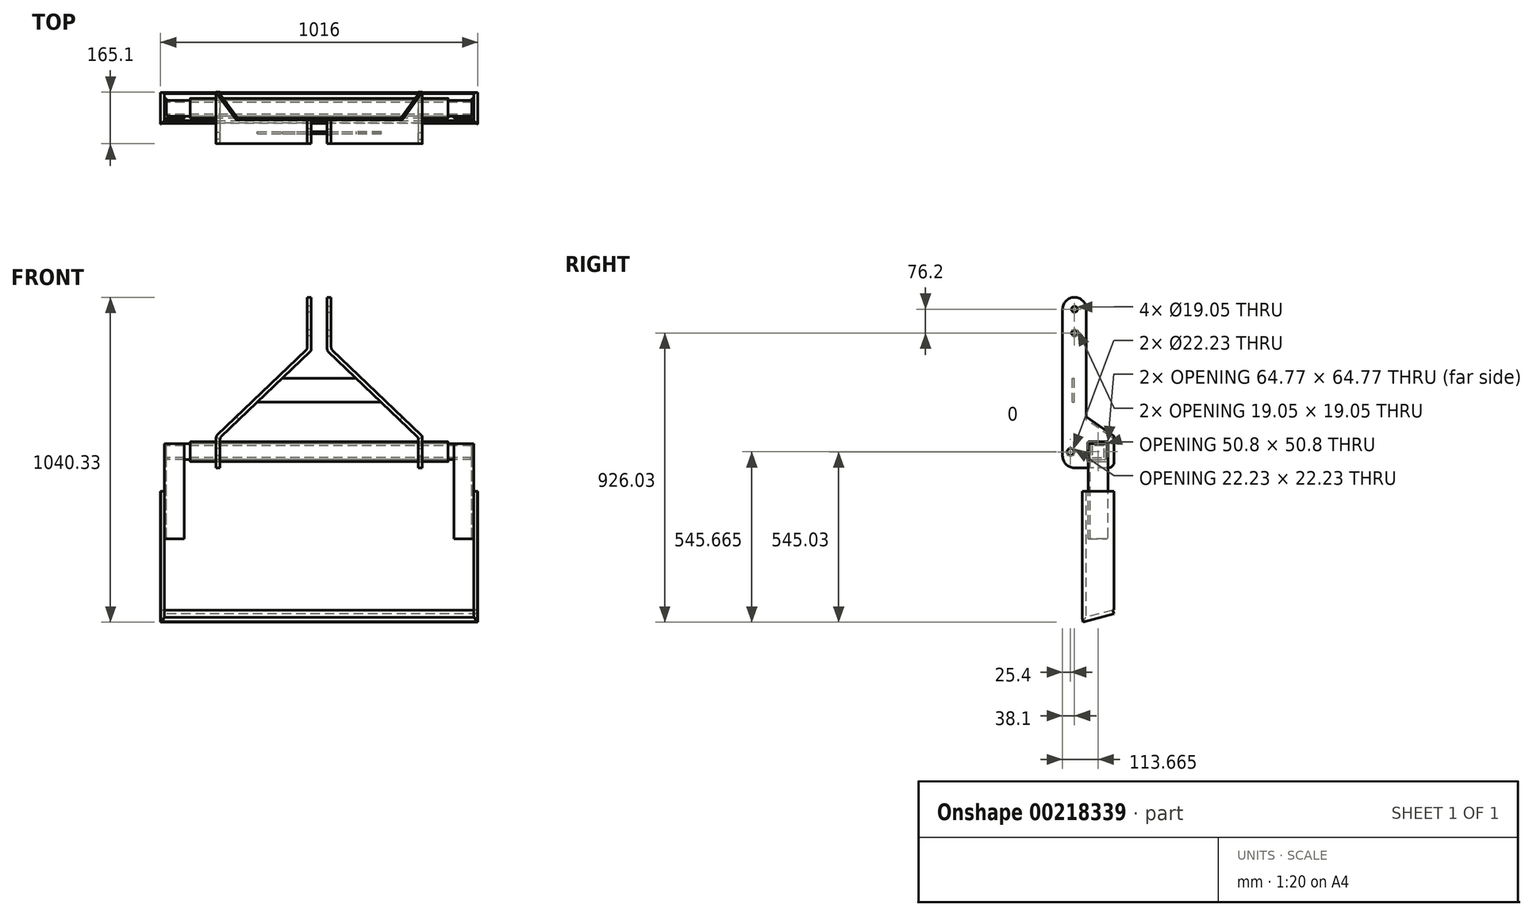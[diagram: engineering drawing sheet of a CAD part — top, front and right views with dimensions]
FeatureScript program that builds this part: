
annotation { "Feature Type Name" : "Feature", "Feature Type Description" : "" }
export const myFeature = defineFeature(function(context is Context, id is Id, definition is map)
    precondition{}
    {
        {
            var Q0;
            Q0=qCreatedBy(makeId("Front.planeOp"),FACE);
            var sketch = newSketch(context, id + "F0", { "sketchPlane" : qUnion([Q0])});
            skLineSegment(sketch, "E0", {"start": v(-330.2, 0) * mm, "end": v(-330.2, 101.6) * mm});
            skLineSegment(sketch, "E1", {"start": v(-330.2, 101.6) * mm, "end": v(-38.1, 381) * mm});
            skLineSegment(sketch, "E2", {"start": v(-38.1, 381) * mm, "end": v(-38.1, 546.1) * mm});
            skLineSegment(sketch, "E3", {"start": v(0, 0) * mm, "end": v(0, 360.93) * mm, "construction": true});
            skLineSegment(sketch, "E4.MirrorCS", {"start": v(38.1, 381) * mm, "end": v(38.1, 546.1) * mm});
            skLineSegment(sketch, "E5.MirrorCS", {"start": v(330.2, 101.6) * mm, "end": v(38.1, 381) * mm});
            skLineSegment(sketch, "E6.MirrorCS", {"start": v(330.2, 0) * mm, "end": v(330.2, 101.6) * mm});
            skSolve(sketch);
        }
        {
            var Q0;
            Q0=qCreatedBy(makeId("Top.planeOp"),FACE);
            var sketch = newSketch(context, id + "F1", { "sketchPlane" : qUnion([Q0])});
            skPoint(sketch, "E7.0", {"position": v(-330.2, 0) * mm});
            skPoint(sketch, "E7.1", {"position": v(330.2, 0) * mm});
            skLineSegment(sketch, "E8", {"start": v(-330.2, 38.1) * mm, "end": v(-330.2, -38.1) * mm});
            skLineSegment(sketch, "E9", {"start": v(0, 137.53) * mm, "end": v(0, -182.2) * mm, "construction": true});
            skLineSegment(sketch, "E10", {"start": v(-330.2, 38.1) * mm, "end": v(-317.5, 38.1) * mm});
            skLineSegment(sketch, "E11", {"start": v(-317.5, 38.1) * mm, "end": v(-317.5, -38.1) * mm});
            skLineSegment(sketch, "E12", {"start": v(-317.5, -38.1) * mm, "end": v(-330.2, -38.1) * mm});
            skSolve(sketch);
        }
        {
            var Q0;
            Q0=makeQuery(id+"F1.imprint","IMPRINT",FACE,{"disambiguationData":[TD([[makeQuery(id+"F1.imprint","IMPRINT",EDGE,{"derivedFrom":sQuery(id+"F1.wireOp",EDGE,"E8")}),1.0]])]});
            var Q1;
            Q1=sQuery(id+"F0.wireOp",EDGE,"E1");
            var Q2;
            Q2=sQuery(id+"F0.wireOp",EDGE,"E0");
            var Q3;
            Q3=sQuery(id+"F0.wireOp",EDGE,"E2");
            sweep(context, id + "F2", {"profiles" : qUnion([Q0]), "path" : qUnion([Q1, Q2, Q3])});
        }
        {
            var Q0;
            Q0=makeQuery(id+"F2.opSweep","SWEPT_FACE",FACE,{"disambiguationData":[OSD([sQuery(id+"F0.wireOp",EDGE,"E0"),sQuery(id+"F1.wireOp",EDGE,"E10")])]});
            var sketch = newSketch(context, id + "F3", { "sketchPlane" : qUnion([Q0])});
            skLineSegment(sketch, "E13.0", {"start": v(330.2, 101.6) * mm, "end": v(38.1, 381) * mm});
            skLineSegment(sketch, "E13.1", {"start": v(317.5, 96.17) * mm, "end": v(25.4, 375.57) * mm});
            skLineSegment(sketch, "E13.2", {"start": v(330.2, 0) * mm, "end": v(330.2, 101.6) * mm});
            skLineSegment(sketch, "E13.3", {"start": v(317.5, 0) * mm, "end": v(317.5, 96.17) * mm});
            skLineSegment(sketch, "E13.4", {"start": v(317.5, 0) * mm, "end": v(330.2, 0) * mm});
            skLineSegment(sketch, "E14", {"start": v(265.96, 163.05) * mm, "end": v(257.18, 153.87) * mm});
            skSolve(sketch);
        }
        {
            var Q0;
            {var subQ0=sQuery(id+"F3.wireOp",EDGE,"E13.2");Q0=makeQuery(id+"F3.imprint","IMPRINT",FACE,{"disambiguationData":[TD([[makeQuery(id+"F3.imprint","IMPRINT",EDGE,{"derivedFrom":subQ0}),1.0]])]});}
            extrude(context, id + "F4", {"entities" : qUnion([Q0]), "operationType" : NewBodyOperationType.ADD, "depth" : 88.9 * mm});
        }
        {
            var Q0;
            Q0=makeQuery(id+"F4.boolean.opBoolean","MERGE",FACE,{"derivedFrom":[makeQuery(id+"F2.opSweep","SWEPT_FACE",FACE,{"disambiguationData":[OSD([sQuery(id+"F0.wireOp",EDGE,"E1"),sQuery(id+"F1.wireOp",EDGE,"E8")])]}),makeQuery(id+"F4.opExtrude","SWEPT_FACE",FACE,{"disambiguationData":[OSD([sQuery(id+"F3.wireOp",EDGE,"E13.0")])]})]});
            var sketch = newSketch(context, id + "F5", { "sketchPlane" : qUnion([Q0])});
            skLineSegment(sketch, "E15.0", {"start": v(-79.49, 127) * mm, "end": v(-79.49, 38.1) * mm});
            skLineSegment(sketch, "E15.1", {"start": v(-168.39, 127) * mm, "end": v(-79.49, 127) * mm});
            skLineSegment(sketch, "E16", {"start": v(-79.49, 38.1) * mm, "end": v(-168.39, 127) * mm});
            skSolve(sketch);
        }
        {
            var Q0;
            Q0=qSketchRegion(id+"F5",true);
            var Q1;
            Q1=makeQuery(id+"F4.boolean.opBoolean","MERGE",FACE,{"derivedFrom":[makeQuery(id+"F2.opSweep","SWEPT_FACE",FACE,{"disambiguationData":[OSD([sQuery(id+"F0.wireOp",EDGE,"E1"),sQuery(id+"F1.wireOp",EDGE,"E11")])]}),makeQuery(id+"F4.opExtrude","SWEPT_FACE",FACE,{"disambiguationData":[OSD([sQuery(id+"F3.wireOp",EDGE,"E13.1")])]})]});
            extrude(context, id + "F6", {"entities" : qUnion([Q0]), "operationType" : NewBodyOperationType.REMOVE, "endBound" : BoundingType.THROUGH_ALL, "oppositeDirection" : true, "endBoundEntityFace" : qUnion([Q1]), "depth" : 25.4 * mm});
        }
        {
            var Q0;
            Q0=makeQuery(id+"F2.opSweep","MID_CAP_EDGE",EDGE,{"disambiguationData":[OSD([sQuery(id+"F0.wireOp",VERTEX,"E0.end"),sQuery(id+"F1.wireOp",EDGE,"E8")])],"capPos":1.0});
            var Q1;
            Q1=makeQuery(id+"F2.opSweep","MID_CAP_EDGE",EDGE,{"disambiguationData":[OSD([sQuery(id+"F0.wireOp",VERTEX,"E0.end"),sQuery(id+"F1.wireOp",EDGE,"E11")])],"capPos":1.0});
            var Q2;
            Q2=makeQuery(id+"F2.opSweep","MID_CAP_EDGE",EDGE,{"disambiguationData":[OSD([sQuery(id+"F0.wireOp",VERTEX,"E2.start"),sQuery(id+"F1.wireOp",EDGE,"E8")])],"capPos":2.0});
            var Q3;
            Q3=makeQuery(id+"F2.opSweep","MID_CAP_EDGE",EDGE,{"disambiguationData":[OSD([sQuery(id+"F0.wireOp",VERTEX,"E2.start"),sQuery(id+"F1.wireOp",EDGE,"E11")])],"capPos":2.0});
            fillet(context, id + "F7", {"entities" : qUnion([Q0, Q1, Q2, Q3]), "radius" : 12.7 * mm, "tangentPropagation" : true, "allowEdgeOverflow" : false});
        }
        {
            var Q0;
            Q0=makeQuery(id+"F2.opSweep","CAP_EDGE",EDGE,{"disambiguationData":[OSD([sQuery(id+"F0.wireOp",VERTEX,"E2.end"),sQuery(id+"F1.wireOp",EDGE,"E12")])],"isStart":false});
            var Q1;
            Q1=makeQuery(id+"F2.opSweep","CAP_EDGE",EDGE,{"disambiguationData":[OSD([sQuery(id+"F0.wireOp",VERTEX,"E2.end"),sQuery(id+"F1.wireOp",EDGE,"E10")])],"isStart":false});
            var Q2;
            Q2=makeQuery(id+"F2.opSweep","CAP_EDGE",EDGE,{"disambiguationData":[OSD([sQuery(id+"F0.wireOp",VERTEX,"E0.start"),sQuery(id+"F1.wireOp",EDGE,"E12")])],"isStart":true});
            fillet(context, id + "F8", {"entities" : qUnion([Q0, Q1, Q2]), "radius" : 38.1 * mm, "tangentPropagation" : true, "allowEdgeOverflow" : false});
        }
        {
            var Q0;
            Q0=makeQuery(id+"F2.opSweep","SWEPT_FACE",FACE,{"disambiguationData":[OSD([sQuery(id+"F0.wireOp",EDGE,"E2"),sQuery(id+"F1.wireOp",EDGE,"E8")])]});
            var sketch = newSketch(context, id + "F9", { "sketchPlane" : qUnion([Q0])});
            skPoint(sketch, "E17.0", {"position": v(0, 546.1) * mm});
            skPoint(sketch, "E17.1", {"position": v(0, 381) * mm});
            skCircle(sketch, "E18", {"center": v(0, 508) * mm, "radius": 9.53 * mm});
            skCircle(sketch, "E19", {"center": v(0, 431.8) * mm, "radius": 9.53 * mm});
            skSolve(sketch);
        }
        {
            var Q0;
            Q0=makeQuery(id+"F9.imprint","IMPRINT",FACE,{"disambiguationData":[TD([[makeQuery(id+"F9.imprint","IMPRINT",EDGE,{"derivedFrom":sQuery(id+"F9.wireOp",EDGE,"E18")}),1.0]])]});
            var Q1;
            Q1=makeQuery(id+"F9.imprint","IMPRINT",FACE,{"disambiguationData":[TD([[makeQuery(id+"F9.imprint","IMPRINT",EDGE,{"derivedFrom":sQuery(id+"F9.wireOp",EDGE,"E19")}),1.0]])]});
            var Q2;
            Q2=makeQuery(id+"F2.opSweep","SWEPT_FACE",FACE,{"disambiguationData":[OSD([sQuery(id+"F0.wireOp",EDGE,"E2"),sQuery(id+"F1.wireOp",EDGE,"E11")])]});
            extrude(context, id + "F10", {"entities" : qUnion([Q0, Q1]), "operationType" : NewBodyOperationType.REMOVE, "endBound" : BoundingType.UP_TO_SURFACE, "oppositeDirection" : true, "endBoundEntityFace" : qUnion([Q2]), "depth" : 25.4 * mm});
        }
        {
            var Q0;
            Q0=makeQuery(id+"F2.opSweep","SWEPT_FACE",FACE,{"disambiguationData":[OSD([sQuery(id+"F0.wireOp",EDGE,"E0"),sQuery(id+"F1.wireOp",EDGE,"E8")])]});
            var sketch = newSketch(context, id + "F11", { "sketchPlane" : qUnion([Q0])});
            skPoint(sketch, "E20.0", {"position": v(0, 101.6) * mm});
            skPoint(sketch, "E20.1", {"position": v(0, 0) * mm});
            skCircle(sketch, "E21", {"center": v(12.7, 50.8) * mm, "radius": 11.11 * mm});
            skLineSegment(sketch, "E22.0", {"start": v(38.1, 38.1) * mm, "end": v(38.1, 96.17) * mm});
            skSolve(sketch);
        }
        {
            var Q0;
            Q0=makeQuery(id+"F11.imprint","IMPRINT",FACE,{"disambiguationData":[TD([[makeQuery(id+"F11.imprint","IMPRINT",EDGE,{"derivedFrom":sQuery(id+"F11.wireOp",EDGE,"E21")}),1.0]])]});
            var Q1;
            Q1=makeQuery(id+"F2.opSweep","SWEPT_FACE",FACE,{"disambiguationData":[OSD([sQuery(id+"F0.wireOp",EDGE,"E0"),sQuery(id+"F1.wireOp",EDGE,"E11")])]});
            extrude(context, id + "F12", {"entities" : qUnion([Q0]), "operationType" : NewBodyOperationType.REMOVE, "endBound" : BoundingType.UP_TO_SURFACE, "oppositeDirection" : true, "endBoundEntityFace" : qUnion([Q1]), "depth" : 25.4 * mm});
        }
        {
            var Q0;
            Q0=makeQuery(id+"F4.opExtrude","CAP_EDGE",EDGE,{"disambiguationData":[OSD([sQuery(id+"F3.wireOp",EDGE,"E13.4")])],"isStart":false});
            var Q1;
            Q1=makeQuery(id+"F6.boolean.opBoolean","COPY",EDGE,{"derivedFrom":makeQuery(id+"F6.opExtrude","SWEPT_EDGE",EDGE,{"disambiguationData":[OSD([sQuery(id+"F0.wireOp",VERTEX,"E0.end"),sQuery(id+"F1.wireOp",EDGE,"E8"),sQuery(id+"F3.wireOp",EDGE,"E13.0"),sQuery(id+"F3.wireOp",EDGE,"E13.2"),sQuery(id+"F5.wireOp",EDGE,"E15.1"),sQuery(id+"F5.wireOp",EDGE,"E16")])]})});
            var Q2;
            Q2=makeQuery(id+"F6.boolean.opBoolean","MERGE",EDGE,{"derivedFrom":[makeQuery(id+"F4.opExtrude","CAP_EDGE",EDGE,{"disambiguationData":[OSD([sQuery(id+"F3.wireOp",EDGE,"E14")])],"isStart":true}),makeQuery(id+"F6.opExtrude","SWEPT_EDGE",EDGE,{"disambiguationData":[OSD([sQuery(id+"F0.wireOp",EDGE,"E1"),sQuery(id+"F1.wireOp",EDGE,"E8"),sQuery(id+"F1.wireOp",EDGE,"E10"),sQuery(id+"F5.wireOp",EDGE,"E15.0"),sQuery(id+"F5.wireOp",EDGE,"E16")])]})]});
            fillet(context, id + "F13", {"entities" : qUnion([Q0, Q1, Q2]), "radius" : 19.05 * mm, "tangentPropagation" : true, "allowEdgeOverflow" : false});
        }
        {
            var Q0;
            Q0=makeQuery(id+"F4.boolean.opBoolean","MERGE",FACE,{"derivedFrom":[makeQuery(id+"F2.opSweep","SWEPT_FACE",FACE,{"disambiguationData":[OSD([sQuery(id+"F0.wireOp",EDGE,"E0"),sQuery(id+"F1.wireOp",EDGE,"E8")])]}),makeQuery(id+"F4.opExtrude","SWEPT_FACE",FACE,{"disambiguationData":[OSD([sQuery(id+"F3.wireOp",EDGE,"E13.2")])]})]});
            var sketch = newSketch(context, id + "F14", { "sketchPlane" : qUnion([Q0])});
            skLineSegment(sketch, "E23.0", {"start": v(-127, 19.05) * mm, "end": v(-127, 90.18) * mm});
            skLineSegment(sketch, "E23.1", {"start": v(-107.95, 0) * mm, "end": v(0, 0) * mm});
            skLineSegment(sketch, "E24", {"start": v(-107.95, 83.82) * mm, "end": v(-107.95, 19.05) * mm});
            skLineSegment(sketch, "E25", {"start": v(-107.95, 19.05) * mm, "end": v(-43.18, 19.05) * mm});
            skLineSegment(sketch, "E26", {"start": v(-43.18, 19.05) * mm, "end": v(-43.18, 83.82) * mm});
            skLineSegment(sketch, "E27", {"start": v(-43.18, 83.82) * mm, "end": v(-107.95, 83.82) * mm});
            skSolve(sketch);
        }
        {
            var Q0;
            Q0=qSketchRegion(id+"F14",true);
            var Q1;
            Q1=makeQuery(id+"F4.boolean.opBoolean","MERGE",FACE,{"derivedFrom":[makeQuery(id+"F2.opSweep","SWEPT_FACE",FACE,{"disambiguationData":[OSD([sQuery(id+"F0.wireOp",EDGE,"E0"),sQuery(id+"F1.wireOp",EDGE,"E11")])]}),makeQuery(id+"F4.opExtrude","SWEPT_FACE",FACE,{"disambiguationData":[OSD([sQuery(id+"F3.wireOp",EDGE,"E13.3")])]})]});
            extrude(context, id + "F15", {"entities" : qUnion([Q0]), "operationType" : NewBodyOperationType.REMOVE, "endBound" : BoundingType.UP_TO_SURFACE, "oppositeDirection" : true, "endBoundEntityFace" : qUnion([Q1]), "depth" : 25.4 * mm});
        }
        {
            var Q0;
            Q0=makeQuery(id+"F15.boolean.opBoolean","COPY",EDGE,{"derivedFrom":makeQuery(id+"F15.opExtrude","SWEPT_EDGE",EDGE,{"disambiguationData":[OSD([sQuery(id+"F14.wireOp",EDGE,"E24"),sQuery(id+"F14.wireOp",EDGE,"E27")])]})});
            var Q1;
            Q1=makeQuery(id+"F15.boolean.opBoolean","COPY",EDGE,{"derivedFrom":makeQuery(id+"F15.opExtrude","SWEPT_EDGE",EDGE,{"disambiguationData":[OSD([sQuery(id+"F14.wireOp",EDGE,"E26"),sQuery(id+"F14.wireOp",EDGE,"E27")])]})});
            var Q2;
            Q2=makeQuery(id+"F15.boolean.opBoolean","COPY",EDGE,{"derivedFrom":makeQuery(id+"F15.opExtrude","SWEPT_EDGE",EDGE,{"disambiguationData":[OSD([sQuery(id+"F14.wireOp",EDGE,"E25"),sQuery(id+"F14.wireOp",EDGE,"E26")])]})});
            var Q3;
            Q3=makeQuery(id+"F15.boolean.opBoolean","COPY",EDGE,{"derivedFrom":makeQuery(id+"F15.opExtrude","SWEPT_EDGE",EDGE,{"disambiguationData":[OSD([sQuery(id+"F14.wireOp",EDGE,"E24"),sQuery(id+"F14.wireOp",EDGE,"E25")])]})});
            fillet(context, id + "F16", {"entities" : qUnion([Q0, Q1, Q2, Q3]), "radius" : 3.17 * mm, "tangentPropagation" : true, "allowEdgeOverflow" : false});
        }
        {
            var Q0;
            Q0=makeQuery(id+"F2.opSweep","SWEPT_BODY",BODY,{"disambiguationData":[OSD([sQuery(id+"F0.wireOp",EDGE,"E0"),sQuery(id+"F1.wireOp",EDGE,"E8"),sQuery(id+"F1.wireOp",EDGE,"E10"),sQuery(id+"F1.wireOp",EDGE,"E11"),sQuery(id+"F1.wireOp",EDGE,"E12")])]});
            var Q1;
            Q1=qCreatedBy(makeId("Right.planeOp"),FACE);
            mirror(context, id + "F17", {"entities" : qUnion([Q0]), "mirrorPlane" : qUnion([Q1])});
        }
        {
            var Q0;
            Q0=qCreatedBy(makeId("Right.planeOp"),FACE);
            var sketch = newSketch(context, id + "F18", { "sketchPlane" : qUnion([Q0])});
            skLineSegment(sketch, "E28.0", {"start": v(46.35, 83.82) * mm, "end": v(104.77, 83.82) * mm, "construction": true});
            skLineSegment(sketch, "E28.1", {"start": v(107.95, 80.65) * mm, "end": v(107.95, 22.22) * mm, "construction": true});
            skLineSegment(sketch, "E28.2", {"start": v(104.77, 19.05) * mm, "end": v(46.35, 19.05) * mm, "construction": true});
            skLineSegment(sketch, "E28.3", {"start": v(43.18, 22.22) * mm, "end": v(43.18, 80.65) * mm, "construction": true});
            skLineSegment(sketch, "E29", {"start": v(75.56, 83.82) * mm, "end": v(75.56, 19.05) * mm, "construction": true});
            skLineSegment(sketch, "E30", {"start": v(107.95, 51.44) * mm, "end": v(43.18, 51.44) * mm, "construction": true});
            skLineSegment(sketch, "E31", {"start": v(107.32, 83.19) * mm, "end": v(43.81, 83.19) * mm});
            skLineSegment(sketch, "E32", {"start": v(43.81, 83.19) * mm, "end": v(43.81, 19.69) * mm});
            skLineSegment(sketch, "E33", {"start": v(43.81, 19.69) * mm, "end": v(107.31, 19.69) * mm});
            skLineSegment(sketch, "E34", {"start": v(107.31, 19.69) * mm, "end": v(107.31, 83.18) * mm});
            skLineSegment(sketch, "E35", {"start": v(100.96, 76.84) * mm, "end": v(50.16, 76.84) * mm});
            skLineSegment(sketch, "E36", {"start": v(50.16, 76.84) * mm, "end": v(50.16, 26.04) * mm});
            skLineSegment(sketch, "E37", {"start": v(50.16, 26.04) * mm, "end": v(100.96, 26.04) * mm});
            skLineSegment(sketch, "E38", {"start": v(100.96, 26.04) * mm, "end": v(100.96, 76.84) * mm});
            skSolve(sketch);
        }
        {
            var Q0;
            Q0=makeQuery(id+"F18.imprint","IMPRINT",FACE,{"disambiguationData":[TD([[makeQuery(id+"F18.imprint","IMPRINT",EDGE,{"derivedFrom":sQuery(id+"F18.wireOp",EDGE,"E31")}),1.0]])]});
            extrude(context, id + "F19", {"entities" : qUnion([Q0]), "endBound" : BoundingType.SYMMETRIC, "depth" : 825.5 * mm});
        }
        {
            var Q0;
            Q0=makeQuery(id+"F19.opExtrude","SWEPT_EDGE",EDGE,{"disambiguationData":[OSD([sQuery(id+"F18.wireOp",EDGE,"E35"),sQuery(id+"F18.wireOp",EDGE,"E38")])]});
            var Q1;
            Q1=makeQuery(id+"F19.opExtrude","SWEPT_EDGE",EDGE,{"disambiguationData":[OSD([sQuery(id+"F18.wireOp",EDGE,"E35"),sQuery(id+"F18.wireOp",EDGE,"E36")])]});
            var Q2;
            Q2=makeQuery(id+"F19.opExtrude","SWEPT_EDGE",EDGE,{"disambiguationData":[OSD([sQuery(id+"F18.wireOp",EDGE,"E36"),sQuery(id+"F18.wireOp",EDGE,"E37")])]});
            var Q3;
            Q3=makeQuery(id+"F19.opExtrude","SWEPT_EDGE",EDGE,{"disambiguationData":[OSD([sQuery(id+"F18.wireOp",EDGE,"E37"),sQuery(id+"F18.wireOp",EDGE,"E38")])]});
            var Q4;
            Q4=makeQuery(id+"F19.opExtrude","SWEPT_EDGE",EDGE,{"disambiguationData":[OSD([sQuery(id+"F18.wireOp",EDGE,"E31"),sQuery(id+"F18.wireOp",EDGE,"E32")])]});
            var Q5;
            Q5=makeQuery(id+"F19.opExtrude","SWEPT_EDGE",EDGE,{"disambiguationData":[OSD([sQuery(id+"F18.wireOp",EDGE,"E32"),sQuery(id+"F18.wireOp",EDGE,"E33")])]});
            var Q6;
            Q6=makeQuery(id+"F19.opExtrude","SWEPT_EDGE",EDGE,{"disambiguationData":[OSD([sQuery(id+"F18.wireOp",EDGE,"E33"),sQuery(id+"F18.wireOp",EDGE,"E34")])]});
            var Q7;
            Q7=makeQuery(id+"F19.opExtrude","SWEPT_EDGE",EDGE,{"disambiguationData":[OSD([sQuery(id+"F18.wireOp",EDGE,"E31"),sQuery(id+"F18.wireOp",EDGE,"E34")])]});
            fillet(context, id + "F20", {"entities" : qUnion([Q0, Q1, Q2, Q3, Q4, Q5, Q6, Q7]), "radius" : 6.35 * mm, "tangentPropagation" : true, "allowEdgeOverflow" : false});
        }
        {
            var Q0;
            Q0=qCreatedBy(makeId("Front.planeOp"),FACE);
            var sketch = newSketch(context, id + "F21", { "sketchPlane" : qUnion([Q0])});
            skLineSegment(sketch, "E39.0", {"start": v(-313.58, 99.92) * mm, "end": v(-29.32, 371.82) * mm});
            skLineSegment(sketch, "E39.1", {"start": v(313.58, 99.92) * mm, "end": v(29.32, 371.82) * mm});
            skLineSegment(sketch, "E39.2", {"start": v(-412.75, 83.19) * mm, "end": v(412.75, 83.19) * mm});
            skLineSegment(sketch, "E40", {"start": v(-118.64, 286.38) * mm, "end": v(118.64, 286.38) * mm});
            skLineSegment(sketch, "E41", {"start": v(-198.3, 210.18) * mm, "end": v(198.3, 210.18) * mm});
            skSolve(sketch);
        }
        {
            var Q0;
            {var subQ0=sQuery(id+"F21.wireOp",EDGE,"E40");Q0=makeQuery(id+"F21.imprint","IMPRINT",FACE,{"disambiguationData":[TD([[makeQuery(id+"F21.imprint","IMPRINT",EDGE,{"derivedFrom":subQ0}),-1.0]])]});}
            extrude(context, id + "F22", {"entities" : qUnion([Q0]), "depth" : 6.35 * mm});
        }
        {
            var Q0;
            Q0=qCreatedBy(makeId("Right.planeOp"),FACE);
            var sketch = newSketch(context, id + "F23", { "sketchPlane" : qUnion([Q0])});
            skLineSegment(sketch, "E42.0", {"start": v(94.61, 76.84) * mm, "end": v(56.51, 76.84) * mm});
            skLineSegment(sketch, "E42.1", {"start": v(100.96, 32.39) * mm, "end": v(100.96, 70.49) * mm});
            skLineSegment(sketch, "E42.2", {"start": v(56.51, 26.04) * mm, "end": v(94.61, 26.04) * mm});
            skLineSegment(sketch, "E42.3", {"start": v(50.16, 70.49) * mm, "end": v(50.16, 32.39) * mm});
            skArc(sketch, "E43.0", {"start": v(56.51, 76.84) * mm, "mid": v(52.02, 74.98) * mm, "end": v(50.16, 70.49) * mm});
            skArc(sketch, "E43.1", {"start": v(100.96, 70.49) * mm, "mid": v(99.1, 74.98) * mm, "end": v(94.61, 76.84) * mm});
            skArc(sketch, "E43.2", {"start": v(94.61, 26.04) * mm, "mid": v(99.1, 27.9) * mm, "end": v(100.96, 32.39) * mm});
            skArc(sketch, "E43.3", {"start": v(50.16, 32.39) * mm, "mid": v(52.02, 27.9) * mm, "end": v(56.51, 26.04) * mm});
            skLineSegment(sketch, "E44", {"start": v(94.61, 70.49) * mm, "end": v(56.51, 70.49) * mm});
            skLineSegment(sketch, "E45", {"start": v(56.52, 70.49) * mm, "end": v(56.51, 32.39) * mm});
            skLineSegment(sketch, "E46", {"start": v(56.51, 32.39) * mm, "end": v(94.61, 32.39) * mm});
            skLineSegment(sketch, "E47", {"start": v(94.61, 32.39) * mm, "end": v(94.61, 70.49) * mm});
            skSolve(sketch);
        }
        {
            var Q0;
            Q0 = qSketchRegion(id + "F23", true);
            extrude(context, id + "F24", {"entities" : qUnion([Q0]), "endBound" : BoundingType.SYMMETRIC, "depth" : 977.9 * mm});
        }
        {
            var Q0;
            Q0=makeQuery(id+"F24.opExtrude","CAP_EDGE",EDGE,{"disambiguationData":[OSD([sQuery(id+"F23.wireOp",EDGE,"E42.3")])],"isStart":true});
            var Q1;
            Q1=makeQuery(id+"F24.opExtrude","CAP_EDGE",EDGE,{"disambiguationData":[OSD([sQuery(id+"F23.wireOp",EDGE,"E42.3")])],"isStart":false});
            fillet(context, id + "F25", {"entities" : qUnion([Q0, Q1]), "radius" : 6.35 * mm, "allowEdgeOverflow" : false});
        }
        {
            var Q0;
            Q0=makeQuery(id+"F24.opExtrude","SWEPT_FACE",FACE,{"disambiguationData":[OSD([sQuery(id+"F23.wireOp",EDGE,"E42.0")])]});
            var sketch = newSketch(context, id + "F26", { "sketchPlane" : qUnion([Q0])});
            skLineSegment(sketch, "E48.0", {"start": v(482.6, 50.16) * mm, "end": v(-482.6, 50.16) * mm});
            skArc(sketch, "E48.1", {"start": v(-488.95, 56.51) * mm, "mid": v(-487.1, 52.02) * mm, "end": v(-482.6, 50.16) * mm});
            skLineSegment(sketch, "E49", {"start": v(-431.8, 50.16) * mm, "end": v(-431.8, 43.81) * mm});
            skLineSegment(sketch, "E50", {"start": v(-431.8, 43.81) * mm, "end": v(-495.3, 43.81) * mm});
            skLineSegment(sketch, "E51", {"start": v(-495.3, 43.81) * mm, "end": v(-495.3, 107.31) * mm});
            skLineSegment(sketch, "E52", {"start": v(-495.3, 107.31) * mm, "end": v(-488.95, 107.31) * mm});
            skLineSegment(sketch, "E53", {"start": v(-488.95, 107.31) * mm, "end": v(-488.95, 56.51) * mm});
            skSolve(sketch);
        }
        {
            var Q0;
            Q0 = qSketchRegion(id + "F26", true);
            extrude(context, id + "F27", {"entities" : qUnion([Q0]), "oppositeDirection" : true, "depth" : 304.8 * mm});
        }
        {
            var Q0;
            Q0=makeQuery(id+"F27.opExtrude","CAP_EDGE",EDGE,{"disambiguationData":[OSD([sQuery(id+"F26.wireOp",EDGE,"E49")])],"isStart":true});
            var Q1;
            Q1=makeQuery(id+"F27.opExtrude","CAP_EDGE",EDGE,{"disambiguationData":[OSD([sQuery(id+"F26.wireOp",EDGE,"E52")])],"isStart":true});
            var Q2;
            Q2=makeQuery(id+"F27.opExtrude","CAP_EDGE",EDGE,{"disambiguationData":[OSD([sQuery(id+"F26.wireOp",EDGE,"E52")])],"isStart":false});
            var Q3;
            Q3=makeQuery(id+"F29.opPattern","COPY",EDGE,{"derivedFrom":makeQuery(id+"F27.opExtrude","CAP_EDGE",EDGE,{"disambiguationData":[OSD([sQuery(id+"F26.wireOp",EDGE,"E52")])],"isStart":false}),"instanceName":"1"});
            var Q4;
            Q4=makeQuery(id+"F29.opPattern","COPY",EDGE,{"derivedFrom":makeQuery(id+"F27.opExtrude","CAP_EDGE",EDGE,{"disambiguationData":[OSD([sQuery(id+"F26.wireOp",EDGE,"E49")])],"isStart":true}),"instanceName":"1"});
            var Q5;
            Q5=makeQuery(id+"F29.opPattern","COPY",EDGE,{"derivedFrom":makeQuery(id+"F27.opExtrude","CAP_EDGE",EDGE,{"disambiguationData":[OSD([sQuery(id+"F26.wireOp",EDGE,"E52")])],"isStart":true}),"instanceName":"1"});
            fillet(context, id + "F28", {"entities" : qUnion([Q0, Q1, Q2, Q3, Q4, Q5]), "radius" : 6.35 * mm, "tangentPropagation" : true, "allowEdgeOverflow" : false});
        }
        {
            var Q0;
            Q0=makeQuery(id+"F27.opExtrude","SWEPT_BODY",BODY,{"disambiguationData":[OSD([sQuery(id+"F26.wireOp",EDGE,"E48.0"),sQuery(id+"F26.wireOp",EDGE,"E48.1"),sQuery(id+"F26.wireOp",EDGE,"E49"),sQuery(id+"F26.wireOp",EDGE,"E50"),sQuery(id+"F26.wireOp",EDGE,"E51"),sQuery(id+"F26.wireOp",EDGE,"E52"),sQuery(id+"F26.wireOp",EDGE,"E53")])]});
            var Q1;
            Q1=qCreatedBy(makeId("Right.planeOp"),FACE);
            mirror(context, id + "F29", {"entities" : qUnion([Q0]), "mirrorPlane" : qUnion([Q1])});
        }
        {
            var Q0;
            Q0=makeQuery(id+"F29.opPattern","COPY",FACE,{"derivedFrom":makeQuery(id+"F27.opExtrude","SWEPT_FACE",FACE,{"disambiguationData":[OSD([sQuery(id+"F26.wireOp",EDGE,"E51")])]}),"instanceName":"1"});
            var sketch = newSketch(context, id + "F30", { "sketchPlane" : qUnion([Q0])});
            skLineSegment(sketch, "E54.0", {"start": v(43.81, -227.97) * mm, "end": v(43.81, 76.83) * mm, "construction": true});
            skLineSegment(sketch, "E55.0", {"start": v(107.31, -221.62) * mm, "end": v(107.31, 70.48) * mm, "construction": true});
            skLineSegment(sketch, "E56", {"start": v(126.36, -75.56) * mm, "end": v(24.76, -75.56) * mm});
            skLineSegment(sketch, "E57", {"start": v(24.76, -75.56) * mm, "end": v(24.77, -481.96) * mm});
            skLineSegment(sketch, "E58", {"start": v(126.36, -75.56) * mm, "end": v(126.36, -454.74) * mm});
            skLineSegment(sketch, "E59", {"start": v(126.37, -454.74) * mm, "end": v(24.76, -481.96) * mm});
            skSolve(sketch);
        }
        {
            var Q0;
            Q0 = qSketchRegion(id + "F30", true);
            extrude(context, id + "F31", {"entities" : qUnion([Q0]), "depth" : 12.7 * mm});
        }
        {
            var Q0;
            Q0=makeQuery(id+"F31.opExtrude","SWEPT_BODY",BODY,{"disambiguationData":[OSD([sQuery(id+"F30.wireOp",EDGE,"E56"),sQuery(id+"F30.wireOp",EDGE,"E57"),sQuery(id+"F30.wireOp",EDGE,"HMrE1xLz-B6wv-OOko-LeQm-jXD5vp173hQ3"),sQuery(id+"F30.wireOp",EDGE,"AgWu94EH-GLxE-wE7v-hsSV-QsDQLW5ssd8M")])]});
            var Q1;
            Q1=qCreatedBy(makeId("Right.planeOp"),FACE);
            mirror(context, id + "F32", {"operationType" : NewBodyOperationType.ADD, "entities" : qUnion([Q0]), "mirrorPlane" : qUnion([Q1])});
        }
        {
            var Q0;
            Q0=makeQuery(id+"F31.opExtrude","SWEPT_FACE",FACE,{"disambiguationData":[OSD([sQuery(id+"F30.wireOp",EDGE,"E59")])]});
            var sketch = newSketch(context, id + "F33", { "sketchPlane" : qUnion([Q0])});
            skLineSegment(sketch, "E60.0", {"start": v(508, -4.36) * mm, "end": v(508, 100.82) * mm, "construction": true});
            skLineSegment(sketch, "E60.1", {"start": v(-508, -4.36) * mm, "end": v(-508, 100.82) * mm, "construction": true});
            skLineSegment(sketch, "E61", {"start": v(508, 100.82) * mm, "end": v(508, -0.78) * mm});
            skLineSegment(sketch, "E62", {"start": v(508, -0.78) * mm, "end": v(-508, -0.78) * mm});
            skLineSegment(sketch, "E63", {"start": v(-508, -0.78) * mm, "end": v(-508, 100.82) * mm});
            skLineSegment(sketch, "E64", {"start": v(508, 100.82) * mm, "end": v(-508, 100.82) * mm});
            skSolve(sketch);
        }
        {
            var Q0;
            Q0 = qSketchRegion(id + "F33", true);
            extrude(context, id + "F34", {"entities" : qUnion([Q0]), "operationType" : NewBodyOperationType.ADD, "depth" : 12.7 * mm});
        }
        {
            var Q0;
            Q0=makeQuery(id+"F32.opPattern","COPY",EDGE,{"derivedFrom":makeQuery(id+"F31.opExtrude","CAP_EDGE",EDGE,{"disambiguationData":[OSD([sQuery(id+"F30.wireOp",EDGE,"E57")])],"isStart":true}),"instanceName":"1"});
            var Q1;
            Q1=makeQuery(id+"F31.opExtrude","CAP_EDGE",EDGE,{"disambiguationData":[OSD([sQuery(id+"F30.wireOp",EDGE,"E57")])],"isStart":true});
            chamfer(context, id + "F35", {"entities" : qUnion([Q0, Q1]), "width" : 11.43 * mm});
        }
        {
            var Q0;
            {var subQ0=makeQuery(id+"F34.opExtrude","CAP_EDGE",EDGE,{"disambiguationData":[OSD([sQuery(id+"F33.wireOp",EDGE,"E64")])],"isStart":true});var subQ1=makeQuery(id+"F31.opExtrude","SWEPT_EDGE",EDGE,{"disambiguationData":[OSD([sQuery(id+"F30.wireOp",EDGE,"E57"),sQuery(id+"F30.wireOp",EDGE,"E59")])]});Q0=makeQuery(id+"F35.opChamfer","MERGE",EDGE,{"derivedFrom":[makeQuery(id+"F34.boolean.opBoolean","MERGE",EDGE,{"derivedFrom":[subQ1,subQ0]}),makeQuery(id+"F34.boolean.opBoolean","MERGE",EDGE,{"derivedFrom":[makeQuery(id+"F32.opPattern","COPY",EDGE,{"derivedFrom":subQ1,"instanceName":"1"}),subQ0]}),makeQuery(id+"F34.boolean.opBoolean","SPLIT",EDGE,{"derivedFrom":subQ0})]});}
            chamfer(context, id + "F36", {"entities" : qUnion([Q0]), "width" : 11.43 * mm, "tangentPropagation" : true});
        }
    });
